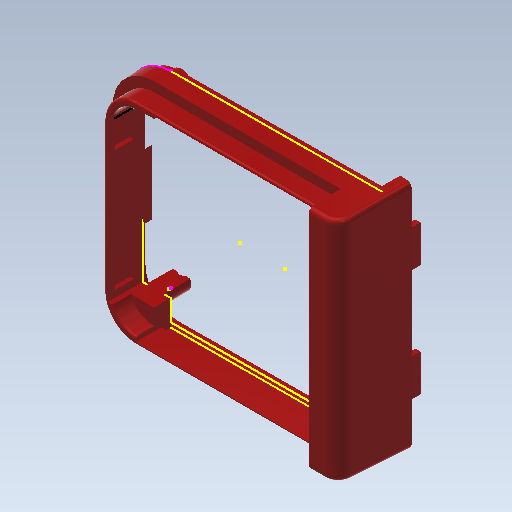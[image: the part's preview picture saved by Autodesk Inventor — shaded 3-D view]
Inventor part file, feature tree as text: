
AUTODESK INVENTOR PART (.ipt)
format: ipt  version: 2020 (Build 240168000, 168)  size: 1,096,192 bytes
history: native  units: in
note: dims shown in document units (in); Inventor stores cm internally (conversion verified against a paired STEP export)
features: sketch x39, extrude x32, reference x10, plane x6, mirror x6, projected_geometry x6, fillet x5, hole x2, loft x1
ambient origin geometry x8: Origin, YZ Plane, XZ Plane, XY Plane, X Axis, Y Axis, Z Axis, Center Point
bodies: Solid1 (feature_tree)
feature tree (107):
  extrude  "Extrusion1"  Depth=0.138in
  fillet  "Fillet1"  Radius=0.064in
  sketch  "Sketch2"  dims[d4=0.064in d9=0.0in d10=90.0deg]
  loft  "Loft2"
  sketch  "Sketch7"  dims[d22=0.0in d23=1.0in d24=0.0in]
  plane  "Work Plane2"
  extrude  "Extrusion2"  Depth=1.0in
  plane  "Work Plane3"
  extrude  "Extrusion4"  Depth=1.0in TaperAngle=0.0deg
  extrude  "Extrusion5"  Depth=0.538in
  extrude  "Extrusion6"  Depth=0.157in TaperAngle=0.0deg
  fillet  "Fillet2"  Radius=0.02in
  extrude  "Extrusion7"  Depth=0.047in
  extrude  "Extrusion9"  Depth=0.168in
  hole  "Hole2"  [1 undecoded]
  plane  "Work Plane4"
  mirror  "Mirror1"
  extrude  "Extrusion10"  Depth=0.303in TaperAngle=0.0deg
  extrude  "Extrusion11"  Depth=0.2771in
  extrude  "Extrusion12"  Depth=0.013in
  extrude  "Extrusion13"  Depth=1.0in TaperAngle=0.0deg
  mirror  "Mirror2"
  sketch  "Sketch24"  dims[d82=0.007in d85=0.079in d86=0.0in d97=0.046in]
  extrude  "Extrusion15"  Depth=0.079in TaperAngle=0.0deg
  sketch  "Sketch26"  dims[d98=0.039in d99=0.0in]
  plane  "Work Plane5"
  sketch  "Sketch27"  dims[d100=0.035in d101=0.193in d102=0.0in]
  fillet  "Fillet3"  Radius=0.046in
  plane  "Work Plane6"
  extrude  "Extrusion17"  TaperAngle=0.0deg  [1 undecoded]
  mirror  "Mirror3"
  extrude  "Extrusion19"  Depth=0.193in TaperAngle=0.0deg
  extrude  "Extrusion20"  Depth=0.461in
  hole  "Hole3"  [1 undecoded]
  extrude  "Extrusion21"  Depth=0.044in
  extrude  "Extrusion22"  Depth=0.059in
  extrude  "Extrusion23"  Depth=0.461in TaperAngle=0.0deg
  mirror  "Mirror4"
  plane  "Work Plane7"
  extrude  "Extrusion24"  Depth=0.461in TaperAngle=0.0deg
  mirror  "Mirror5"
  extrude  "Extrusion25"  Depth=0.098in TaperAngle=0.0deg
  fillet  "Fillet4"  Radius=0.008in
  extrude  "Extrusion27"  Depth=0.217in
  fillet  "Fillet6"  Radius=1.0in
  mirror  "Mirror6"
  extrude  "Extrusion30"  Depth=0.059in TaperAngle=0.0deg
  sketch  "Sketch40"  dims[d166=0.078in d167=0.0in d168=0.62in]
  extrude  "Extrusion31"  Depth=1.0in TaperAngle=0.0deg
  sketch  "Sketch42"  dims[d172=0.01in d173=0.0in d174=0.01in d175=0.0in]
  extrude  "Extrusion32"  Depth=0.078in TaperAngle=0.0deg
  extrude  "Extrusion33"  Depth=0.62in
  sketch  "Sketch43"
  sketch  "Sketch44"
  extrude  "Extrusion34"  Depth=0.078in TaperAngle=0.0deg
  extrude  "Extrusion35"  Depth=0.01in TaperAngle=0.0deg
  sketch  "Sketch47"
  extrude  "Extrusion37"  [1 undecoded]
  extrude  "Extrusion38"  [1 undecoded]
  extrude  "Extrusion39"  [1 undecoded]
  extrude  "Extrusion40"  [1 undecoded]
  extrude  "Extrusion41"  [1 undecoded]
  sketch  "Sketch1"  dims[d0=0.138in d1=-0.0137in d2=0.354in d3=0.064in]
  sketch  "Sketch3"  dims[d11=0.0in d12=90.0deg d18=1.0in d19=0.0137in]
  sketch  "Sketch9"  dims[d25=1.0in d26=0.0in d27=0.538in d28=0.4198in]
  reference  "Reference5"
  sketch  "Sketch10"  dims[d29=0.354in d30=0.157in d31=0.0in d32=0.02in]
  projected_geometry  "Projected Loop4"
  sketch  "Sketch11"  dims[d33=0.157in d34=0.0in d49=0.047in]
  sketch  "Sketch12"  dims[d50=0.079in d51=0.168in]
  sketch  "Sketch15"  dims[d52=0.225in d53=-0.0034in]
  reference  "Reference7"
  reference  "Reference8"
  reference  "Reference9"
  sketch  "Sketch16"  dims[d54=0.067in d55=0.75in d56=0.106in d57=0.25in d58=0.5635in d59=0.25in d60=0.8108in d61=0.281in]
  sketch  "Sketch17"  dims[d62=0.223in d63=0.303in d64=0.0in]
  sketch  "Sketch19"  dims[d65=0.281in d71=0.2771in]
  reference  "Reference10"
  sketch  "Sketch21"  dims[d73=0.079in d74=0.0in d77=0.013in]
  sketch  "Sketch22"  dims[d78=0.079in d79=0.0in d80=1.0in d81=0.0in]
  sketch  "Sketch28"  dims[d105=0.182in d106=0.0in d108=0.461in d109=-0.0034in]
  sketch  "Sketch29"  dims[d110=0.066in d111=0.75in d112=0.106in d113=0.25in d114=135.0deg d115=1.0in d116=0.0in d117=0.6219in]
  sketch  "Sketch30"  dims[d118=0.461in d119=0.0in d120=0.044in]
  reference  "Reference11"
  sketch  "Sketch31"  dims[d121=0.461in d122=0.0in d123=0.059in]
  sketch  "Sketch32"  dims[d124=0.461in d125=0.0in d126=0.461in d127=0.0in]
  sketch  "Sketch33"  dims[d128=0.059in d129=0.461in d130=0.0in]
  sketch  "Sketch34"  dims[d131=0.059in d134=0.098in d135=0.0in d137=0.008in]
  sketch  "Sketch35"  dims[d146=1.0in d147=0.0in d148=0.217in d149=1.0in d150=0.0in]
  sketch  "Sketch36"  dims[d151=0.079in d152=0.0in d153=0.059in d154=0.0in]
  sketch  "Sketch37"  dims[d155=0.039in d156=1.0in d157=0.0in]
  sketch  "Sketch38"  dims[d158=1.0in d159=0.0in d164=0.078in d165=0.0in]
  reference  "Reference12"
  reference  "Reference13"
  reference  "Reference14"
  reference  "Reference15"
  sketch  "Sketch41"  dims[d169=0.047in d170=0.078in d171=0.0in]
  projected_geometry  "Projected Loop7"
  sketch  "Sketch45"
  sketch  "Sketch46"
  sketch  "Sketch48"
  sketch  "Sketch49"
  sketch  "Sketch50"
  projected_geometry  "Project Cut Edges2"
  projected_geometry  "Project Cut Edges3"
  projected_geometry  "Project Cut Edges4"
  projected_geometry  "Project Cut Edges5"
note: 8 required parameter values undecoded (feature->parameter linkage not recoverable at this tier; creation-order binding heuristic only, values carry confidence <= 0.55)
